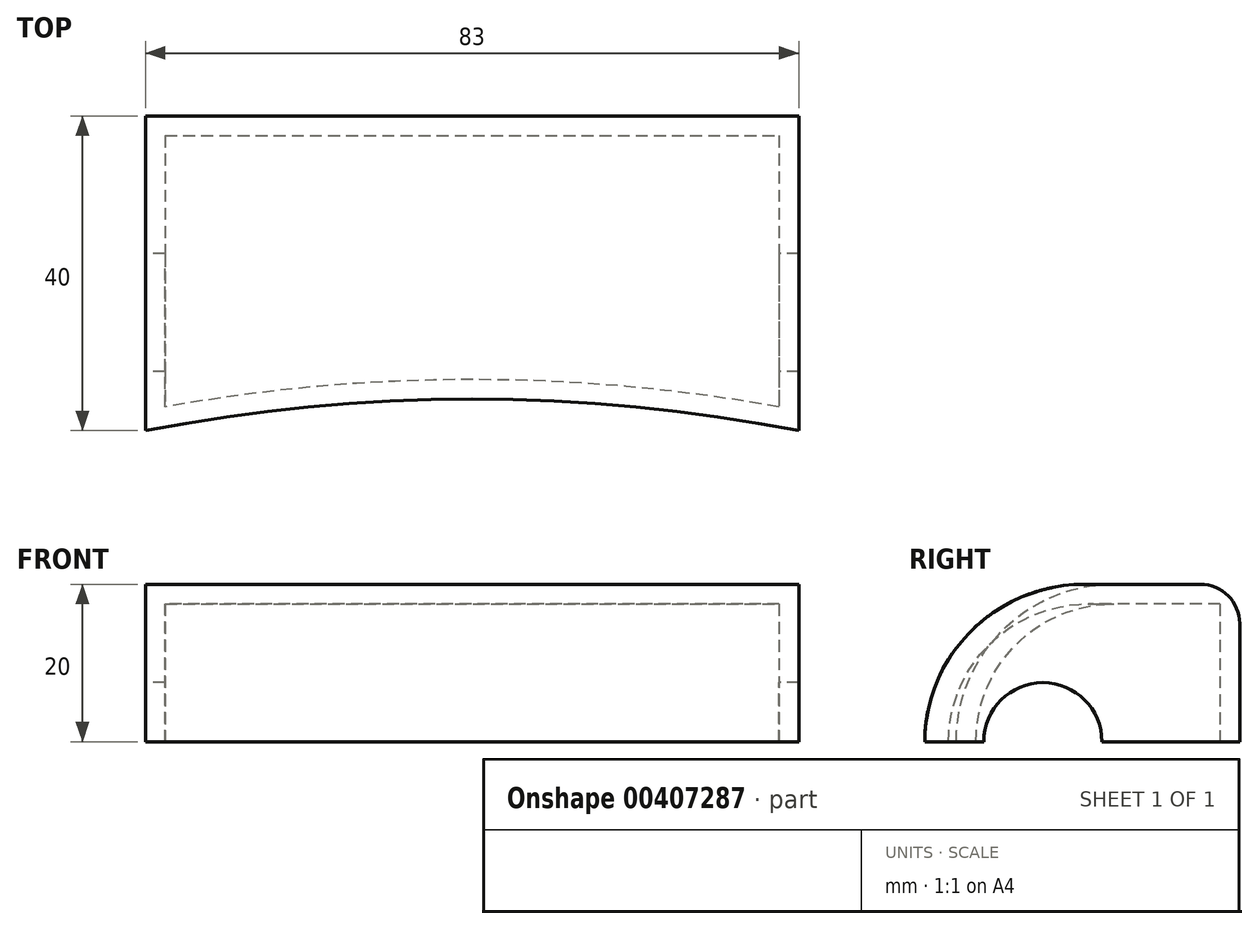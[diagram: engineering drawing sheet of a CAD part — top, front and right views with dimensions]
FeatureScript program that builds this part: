
annotation { "Feature Type Name" : "Feature", "Feature Type Description" : "" }
export const myFeature = defineFeature(function(context is Context, id is Id, definition is map)
    precondition{}
    {
        {
            var Q0;
            Q0=qCreatedBy(makeId("Top.planeOp"),FACE);
            var sketch = newSketch(context, id + "F0", { "sketchPlane" : qUnion([Q0])});
            skLineSegment(sketch, "E0.bottom", {"start": v(0, 0) * mm, "end": v(83, 0) * mm});
            skLineSegment(sketch, "E0.left", {"start": v(0, 0) * mm, "end": v(0, -40) * mm});
            skLineSegment(sketch, "E0.right", {"start": v(83, 0) * mm, "end": v(83, -40) * mm});
            skArc(sketch, "E1", {"start": v(83, -40) * mm, "mid": v(41.5, -36) * mm, "end": v(0, -40) * mm});
            skSolve(sketch);
        }
        {
            var Q0;
            Q0=makeQuery(id+"F0.imprint","IMPRINT",FACE,{"disambiguationData":[TD([[makeQuery(id+"F0.imprint","IMPRINT",EDGE,{"derivedFrom":sQuery(id+"F0.wireOp",EDGE,"E0.bottom")}),-1.0]])]});
            extrude(context, id + "F1", {"entities" : qUnion([Q0]), "depth" : 20 * mm});
        }
        {
            var Q0;
            Q0=makeQuery(id+"F1.opExtrude","CAP_EDGE",EDGE,{"disambiguationData":[OSD([sQuery(id+"F0.wireOp",EDGE,"E1")])],"isStart":false});
            fillet(context, id + "F2", {"entities" : qUnion([Q0]), "radius" : 20 * mm, "tangentPropagation" : true, "allowEdgeOverflow" : false});
        }
        {
            var Q0;
            Q0=makeQuery(id+"F1.opExtrude","CAP_FACE",FACE,{"disambiguationData":[OSD([sQuery(id+"F0.wireOp",EDGE,"E0.bottom"),sQuery(id+"F0.wireOp",EDGE,"E0.left"),sQuery(id+"F0.wireOp",EDGE,"E0.right"),sQuery(id+"F0.wireOp",EDGE,"E1")])],"isStart":true});
            shell(context, id + "F3", {"entities" : qUnion([Q0]), "thickness" : 2.5 * mm});
        }
        {
            var Q0;
            Q0=makeQuery(id+"F1.opExtrude","CAP_EDGE",EDGE,{"disambiguationData":[OSD([sQuery(id+"F0.wireOp",EDGE,"E0.bottom")])],"isStart":false});
            fillet(context, id + "F4", {"entities" : qUnion([Q0]), "radius" : 5 * mm, "tangentPropagation" : true, "allowEdgeOverflow" : false});
        }
        {
            var Q0;
            Q0=qCreatedBy(makeId("Right.planeOp"),FACE);
            var sketch = newSketch(context, id + "F5", { "sketchPlane" : qUnion([Q0])});
            skLineSegment(sketch, "E2", {"start": v(0, 0) * mm, "end": v(-25, 0) * mm});
            skCircle(sketch, "E3", {"center": v(-25, 0) * mm, "radius": 7.5 * mm});
            skSolve(sketch);
        }
        {
            var Q0;
            Q0 = qSketchRegion(id + "F5", true);
            extrude(context, id + "F6", {"entities" : qUnion([Q0]), "operationType" : NewBodyOperationType.REMOVE, "depth" : 83 * mm});
        }
    });
